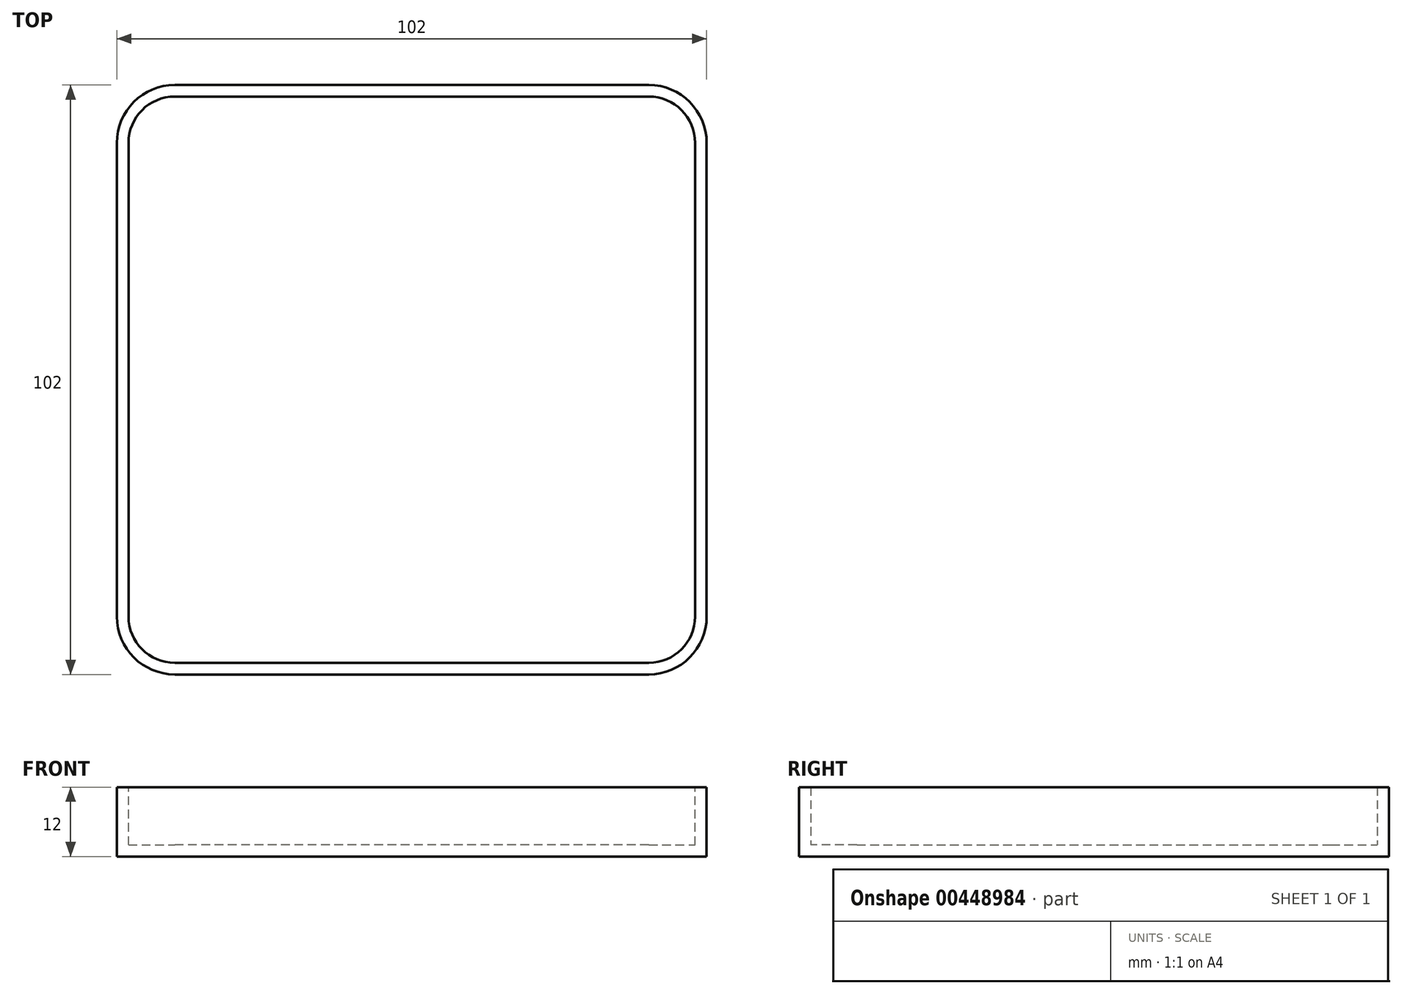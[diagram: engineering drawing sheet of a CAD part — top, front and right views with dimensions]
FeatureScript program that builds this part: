
annotation { "Feature Type Name" : "Feature", "Feature Type Description" : "" }
export const myFeature = defineFeature(function(context is Context, id is Id, definition is map)
    precondition{}
    {
        {
            var Q0;
            Q0=qCreatedBy(makeId("Top.planeOp"),FACE);
            var sketch = newSketch(context, id + "F0", { "sketchPlane" : qUnion([Q0])});
            skLineSegment(sketch, "E0.bottom", {"start": v(51, -51) * mm, "end": v(-51, -51) * mm});
            skLineSegment(sketch, "E0.top", {"start": v(51, 51) * mm, "end": v(-51, 51) * mm});
            skLineSegment(sketch, "E0.left", {"start": v(51, -51) * mm, "end": v(51, 51) * mm});
            skLineSegment(sketch, "E0.right", {"start": v(-51, -51) * mm, "end": v(-51, 51) * mm});
            skPoint(sketch, "E0.middle", {"position": v(0, 0) * mm});
            skSolve(sketch);
        }
        {
            var Q0;
            Q0 = qSketchRegion(id + "F0", true);
            extrude(context, id + "F1", {"entities" : qUnion([Q0]), "depth" : 12 * mm});
        }
        {
            var Q0;
            Q0=makeQuery(id+"F1.opExtrude","SWEPT_EDGE",EDGE,{"disambiguationData":[OSD([sQuery(id+"F0.wireOp",EDGE,"E0.bottom"),sQuery(id+"F0.wireOp",EDGE,"E0.right")])]});
            var Q1;
            Q1=makeQuery(id+"F1.opExtrude","SWEPT_EDGE",EDGE,{"disambiguationData":[OSD([sQuery(id+"F0.wireOp",EDGE,"E0.bottom"),sQuery(id+"F0.wireOp",EDGE,"E0.left")])]});
            var Q2;
            Q2=makeQuery(id+"F1.opExtrude","SWEPT_EDGE",EDGE,{"disambiguationData":[OSD([sQuery(id+"F0.wireOp",EDGE,"E0.top"),sQuery(id+"F0.wireOp",EDGE,"E0.left")])]});
            var Q3;
            Q3=makeQuery(id+"F1.opExtrude","SWEPT_EDGE",EDGE,{"disambiguationData":[OSD([sQuery(id+"F0.wireOp",EDGE,"E0.top"),sQuery(id+"F0.wireOp",EDGE,"E0.right")])]});
            fillet(context, id + "F2", {"entities" : qUnion([Q0, Q1, Q2, Q3]), "radius" : 10 * mm, "tangentPropagation" : true, "allowEdgeOverflow" : false});
        }
        {
            var Q0;
            Q0=makeQuery(id+"F1.opExtrude","CAP_FACE",FACE,{"disambiguationData":[OSD([sQuery(id+"F0.wireOp",EDGE,"E0.bottom"),sQuery(id+"F0.wireOp",EDGE,"E0.top"),sQuery(id+"F0.wireOp",EDGE,"E0.left"),sQuery(id+"F0.wireOp",EDGE,"E0.right")])],"isStart":false});
            shell(context, id + "F3", {"entities" : qUnion([Q0]), "thickness" : 2 * mm});
        }
    });
